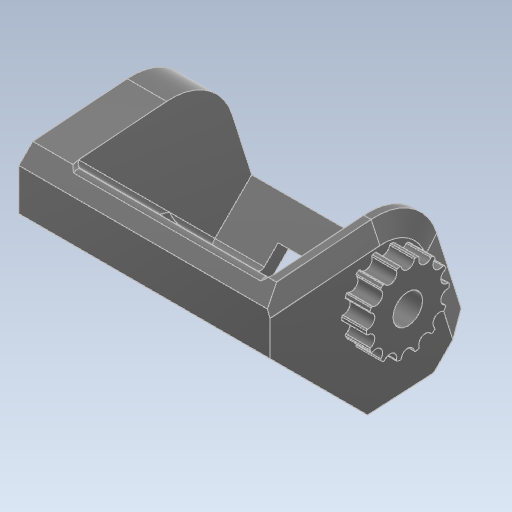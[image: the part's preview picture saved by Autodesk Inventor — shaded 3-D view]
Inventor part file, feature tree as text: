
AUTODESK INVENTOR PART (.ipt)
format: ipt  version: 2024 (Build 280153000, 153)  size: 357,376 bytes
history: native  units: mm
features: other x11, extrude x3, sketch x1, chamfer x1, fillet x1, projected_geometry x1
ambient origin geometry x8: Origin, YZ Plane, XZ Plane, XY Plane, X Axis, Y Axis, Z Axis, Center Point
bodies: Solid1 (feature_tree)
feature tree (18):
  other  "_bridseye_sketch.ipt"
  other  "brideye_wristUnit_pully-origin.ipt"
  sketch  "スケッチ4"
  other  "measure"
  other  "measure2"
  other  "ボディを移動1"
  other  "結合1"
  chamfer  "面取り3"  Distance=10.0mm
  fillet  "フィレット1"  Radius=10.0mm
  extrude  "押し出し1"  Depth=14.0mm
  extrude  "押し出し2"  Depth=43.758794mm
  extrude  "押し出し3"  Depth=0.5mm
  other  "ソリッド31::_bridseye_sketch.ipt"
  other  "TaggingFeature1"
  other  "Solid1::brideye_wristUnit_pully-origin.ipt"
  other  "TaggingFeature2"
  projected_geometry  "投影ループ1"
  other  "ソリッド31"
